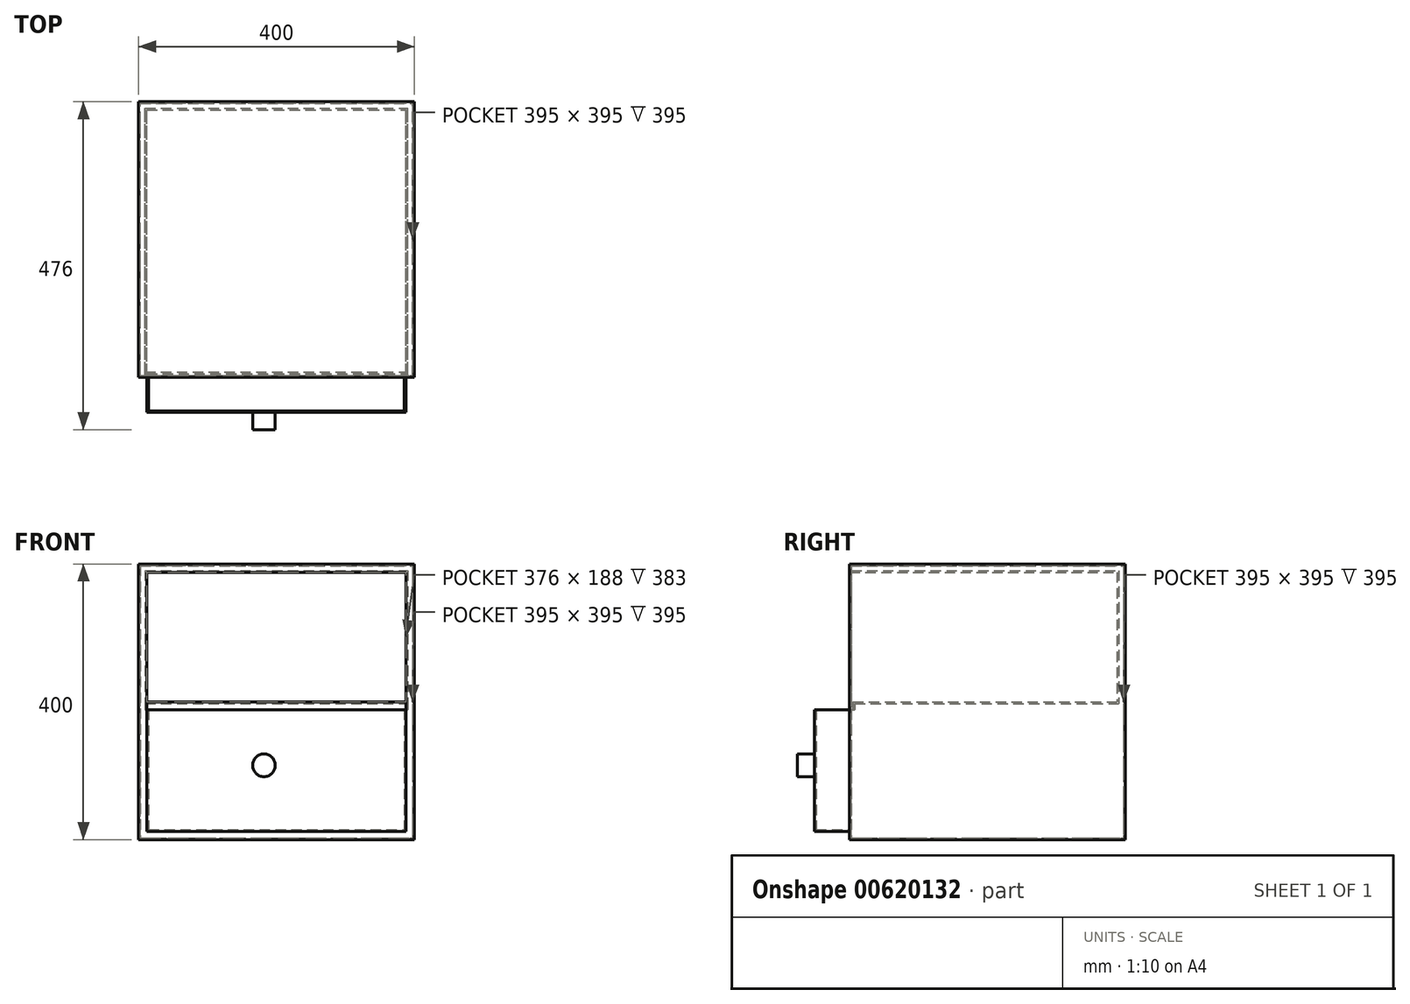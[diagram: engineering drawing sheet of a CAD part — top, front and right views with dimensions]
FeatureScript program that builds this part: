
annotation { "Feature Type Name" : "Feature", "Feature Type Description" : "" }
export const myFeature = defineFeature(function(context is Context, id is Id, definition is map)
    precondition{}
    {
        {
            var Q0;
            Q0=qCreatedBy(makeId("Top.planeOp"),FACE);
            var sketch = newSketch(context, id + "F0", { "sketchPlane" : qUnion([Q0])});
            skLineSegment(sketch, "E0.bottom", {"start": v(-204, -111.1) * mm, "end": v(196, -111.1) * mm});
            skLineSegment(sketch, "E0.top", {"start": v(-204, 288.9) * mm, "end": v(196, 288.9) * mm});
            skLineSegment(sketch, "E0.left", {"start": v(-204, -111.1) * mm, "end": v(-204, 288.9) * mm});
            skLineSegment(sketch, "E0.right", {"start": v(196, -111.1) * mm, "end": v(196, 288.9) * mm});
            skSolve(sketch);
        }
        {
            var Q0;
            Q0=qSketchRegion(id+"F0",true);
            extrude(context, id + "F1", {"entities" : qUnion([Q0]), "depth" : 400 * mm});
        }
        {
            var Q0;
            Q0=makeQuery(id+"F1.opExtrude","SWEPT_FACE",FACE,{"disambiguationData":[OSD([sQuery(id+"F0.wireOp",EDGE,"E0.bottom")])]});
            shell(context, id + "F2", {"entities" : qUnion([Q0]), "thickness" : 12 * mm});
        }
        {
            var Q0;
            Q0=makeQuery(id+"F2.opShell","OFFSET_FACE",FACE,{"disambiguationData":[OSD([sQuery(id+"F0.wireOp",EDGE,"E0.top")])]});
            var sketch = newSketch(context, id + "F3", { "sketchPlane" : qUnion([Q0])});
            skLineSegment(sketch, "E1.bottom", {"start": v(-12.44, 388) * mm, "end": v(0, 388) * mm});
            skLineSegment(sketch, "E1.top", {"start": v(-12.44, 203.75) * mm, "end": v(0, 203.75) * mm});
            skLineSegment(sketch, "E1.left", {"start": v(-12.44, 388) * mm, "end": v(-12.44, 203.75) * mm});
            skLineSegment(sketch, "E1.right", {"start": v(0, 388) * mm, "end": v(0, 203.75) * mm});
            skSolve(sketch);
        }
        {
            var Q0;
            Q0=makeQuery(id+"F2.opShell","OFFSET_FACE",FACE,{"disambiguationData":[OSD([sQuery(id+"F0.wireOp",EDGE,"E0.top")])]});
            var sketch = newSketch(context, id + "F4", { "sketchPlane" : qUnion([Q0])});
            skLineSegment(sketch, "E2.bottom", {"start": v(-192, 200) * mm, "end": v(184, 200) * mm});
            skLineSegment(sketch, "E2.top", {"start": v(-192, 188.75) * mm, "end": v(184, 188.75) * mm});
            skLineSegment(sketch, "E2.left", {"start": v(-192, 200) * mm, "end": v(-192, 188.75) * mm});
            skLineSegment(sketch, "E2.right", {"start": v(184, 200) * mm, "end": v(184, 188.75) * mm});
            skSolve(sketch);
        }
        {
            var Q0;
            Q0=qSketchRegion(id+"F4",true);
            extrude(context, id + "F5", {"entities" : qUnion([Q0]), "operationType" : NewBodyOperationType.ADD, "depth" : 383 * mm});
        }
        {
            var Q0;
            {var subQ2=sQuery(id+"F0.wireOp",EDGE,"E0.top");Q0=makeQuery(id+"F5.boolean.opBoolean","SPLIT",FACE,{"disambiguationData":[TD([makeQuery(id+"F5.opExtrude","SWEPT_FACE",FACE,{"disambiguationData":[OSD([sQuery(id+"F4.wireOp",EDGE,"E2.top")])]})])],"derivedFrom":makeQuery(id+"F2.opShell","OFFSET_FACE",FACE,{"disambiguationData":[OSD([subQ2])]})});}
            var sketch = newSketch(context, id + "F6", { "sketchPlane" : qUnion([Q0])});
            skLineSegment(sketch, "E3.bottom", {"start": v(-192, 188.75) * mm, "end": v(184, 188.75) * mm});
            skLineSegment(sketch, "E3.top", {"start": v(-192, 12) * mm, "end": v(184, 12) * mm});
            skLineSegment(sketch, "E3.left", {"start": v(-192, 188.75) * mm, "end": v(-192, 12) * mm});
            skLineSegment(sketch, "E3.right", {"start": v(184, 188.75) * mm, "end": v(184, 12) * mm});
            skSolve(sketch);
        }
        {
            var Q0;
            Q0=qSketchRegion(id+"F6",true);
            extrude(context, id + "F7", {"entities" : qUnion([Q0]), "operationType" : NewBodyOperationType.ADD, "depth" : 439 * mm});
        }
        {
            var Q0;
            Q0=makeQuery(id+"F7.opExtrude","SWEPT_FACE",FACE,{"disambiguationData":[OSD([sQuery(id+"F6.wireOp",EDGE,"E3.bottom")])]});
            shell(context, id + "F8", {"entities" : qUnion([Q0]), "thickness" : 2.5 * mm});
        }
        {
            var Q0;
            Q0=makeQuery(id+"F7.opExtrude","CAP_FACE",FACE,{"disambiguationData":[OSD([sQuery(id+"F6.wireOp",EDGE,"E3.bottom"),sQuery(id+"F6.wireOp",EDGE,"E3.top"),sQuery(id+"F6.wireOp",EDGE,"E3.left"),sQuery(id+"F6.wireOp",EDGE,"E3.right")])],"isStart":false});
            var sketch = newSketch(context, id + "F9", { "sketchPlane" : qUnion([Q0])});
            skCircle(sketch, "E4", {"center": v(-22.2, 107.93) * mm, "radius": 16.45 * mm});
            skSolve(sketch);
        }
        {
            var Q0;
            Q0=qSketchRegion(id+"F9",true);
            extrude(context, id + "F10", {"entities" : qUnion([Q0]), "operationType" : NewBodyOperationType.ADD, "depth" : 25 * mm});
        }
    });
